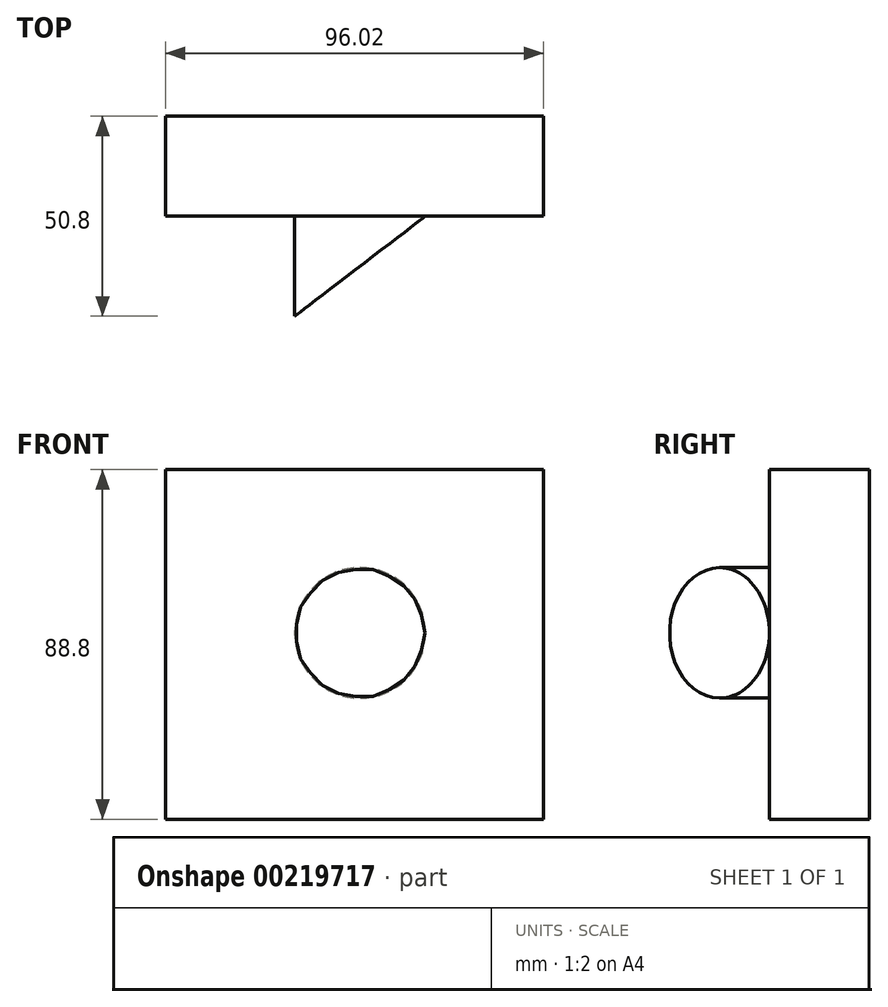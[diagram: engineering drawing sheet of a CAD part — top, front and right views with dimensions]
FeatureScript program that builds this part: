
annotation { "Feature Type Name" : "Feature", "Feature Type Description" : "" }
export const myFeature = defineFeature(function(context is Context, id is Id, definition is map)
    precondition{}
    {
        {
            var Q0;
            Q0=qCreatedBy(makeId("Front.planeOp"),FACE);
            var sketch = newSketch(context, id + "F0", { "sketchPlane" : qUnion([Q0])});
            skLineSegment(sketch, "E0.bottom", {"start": v(-48.01, 44.4) * mm, "end": v(48.01, 44.4) * mm});
            skLineSegment(sketch, "E0.top", {"start": v(-48.01, -44.4) * mm, "end": v(48.01, -44.4) * mm});
            skLineSegment(sketch, "E0.left", {"start": v(-48.01, 44.4) * mm, "end": v(-48.01, -44.4) * mm});
            skLineSegment(sketch, "E0.right", {"start": v(48.01, 44.4) * mm, "end": v(48.01, -44.4) * mm});
            skPoint(sketch, "E0.middle", {"position": v(0, 0) * mm});
            skSolve(sketch);
        }
        {
            var Q0;
            Q0=makeQuery(id+"F0.imprint","IMPRINT",FACE,{"disambiguationData":[TD([[makeQuery(id+"F0.imprint","IMPRINT",EDGE,{"derivedFrom":sQuery(id+"F0.wireOp",EDGE,"E0.bottom")}),-1.0]])]});
            extrude(context, id + "F1", {"entities" : qUnion([Q0]), "depth" : 25.4 * mm});
        }
        {
            var Q0;
            Q0=makeQuery(id+"F1.opExtrude","CAP_FACE",FACE,{"disambiguationData":[OSD([sQuery(id+"F0.wireOp",EDGE,"E0.bottom"),sQuery(id+"F0.wireOp",EDGE,"E0.top"),sQuery(id+"F0.wireOp",EDGE,"E0.left"),sQuery(id+"F0.wireOp",EDGE,"E0.right")])],"isStart":false});
            var sketch = newSketch(context, id + "F2", { "sketchPlane" : qUnion([Q0])});
            skCircle(sketch, "E1", {"center": v(1.38, 2.94) * mm, "radius": 16.58 * mm});
            skPoint(sketch, "E1.first.point", {"position": v(9.15, 17.59) * mm});
            skPoint(sketch, "E1.second.point", {"position": v(-8.24, -10.57) * mm});
            skPoint(sketch, "E1.third.point", {"position": v(16.1, -4.69) * mm});
            skSolve(sketch);
        }
        {
            var Q0;
            Q0=makeQuery(id+"F2.imprint","IMPRINT",FACE,{"disambiguationData":[TD([[makeQuery(id+"F2.imprint","IMPRINT",EDGE,{"derivedFrom":sQuery(id+"F2.wireOp",EDGE,"E1")}),1.0]])]});
            extrude(context, id + "F3", {"entities" : qUnion([Q0]), "operationType" : NewBodyOperationType.ADD, "depth" : 25.4 * mm});
        }
        {
            var Q0;
            Q0=makeQuery(id+"F1.opExtrude","SWEPT_FACE",FACE,{"disambiguationData":[OSD([sQuery(id+"F0.wireOp",EDGE,"E0.top")])]});
            var sketch = newSketch(context, id + "F4", { "sketchPlane" : qUnion([Q0])});
            skLineSegment(sketch, "E2.0", {"start": v(-15.2, 50.8) * mm, "end": v(17.96, 50.8) * mm});
            skLineSegment(sketch, "E3", {"start": v(17.96, 50.8) * mm, "end": v(17.96, 25.4) * mm});
            skLineSegment(sketch, "E4", {"start": v(-15.2, 50.8) * mm, "end": v(17.96, 25.4) * mm});
            skSolve(sketch);
        }
        {
            var Q0;
            Q0 = qSketchRegion(id + "F4", true);
            extrude(context, id + "F5", {"entities" : qUnion([Q0]), "operationType" : NewBodyOperationType.REMOVE, "endBound" : BoundingType.THROUGH_ALL, "oppositeDirection" : true, "depth" : 25.4 * mm});
        }
    });
